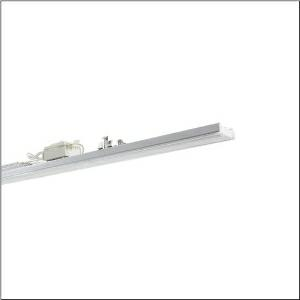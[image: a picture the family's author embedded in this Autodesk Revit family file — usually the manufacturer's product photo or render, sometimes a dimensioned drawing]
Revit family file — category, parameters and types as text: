
# Revit family: licross_r__21_recessed_ho_52te12dn4fxm3s4_e70e
name_source: partatom
category: Lighting Fixtures
units: mm (PartAtom-declared; Revit-internal decimal feet)

## family parameters
Cut with Voids When Loaded = No
Host = Face
Light Source = No
Part Type = Normal
Room Calculation Point = No
Round Connector Dimension = Use Diameter
Shared = No

## types (1)
- --- (1 x LED, 930 lm, 7.5 W, 4000K)
    Apparent Load = 8 VA
    CIE Flux Codes = 69 91 98 100 100
    Color Rendering = 80
    Color Temperature = 4000K
    Default Elevation = 1800 mm
    Description = Licross® 21 Recessed HO, luminaire insert, of sheet steel, galvanised, coil coated, white, length: 1.500mm, width: 66mm, height: 67mm, LED rated luminous flux: 15.000lm, light colour: 840, control gear: DALI 2, with plug, 6-pole, with phase selection, for trunking rail, 9 or 11-core, mains connection: 220..240V, AC, 50/60Hz, rated input power: 88W, internal wiring halogen-free, for emergency light function, for trunking rail, 9-/11-core, converter,control gear: single battery element, battery: LiFePO4, 9Ah, primary optical cover: cover, of PMMA, light emission: direct distribution, primary light characteristic: symmetric, protection rating (complete): IP54, insulation class (complete): insulation class I (protective earthing), certification: CE, UKCA, protection symbol: D if used in an environment with non-conductive dust loads with corresponding accessories, impact resistance: IK06, permissible ambient temperature for indoor applications: +5..+30°C, standard: EN 60598-2-22, LABS conformity tested according to VDMA 24364:2018-05, reducing of maximum allowable ambient temperature of 5°C with ceiling mounting, corresponds to IFS (International Featured Standards) requirements for safety and quality in the food industry, packaging unit: 1 piece
    Height = 58 mm
    Lamp = 1 x LED
    Lamp Light Flux = 930 lm
    Lamp Power = 7.5 W
    Lamp count = 1
    Length = 1500 mm
    Luminous efficacy = 124 lm/W
    Manufacturer = Siteco
    ModVariant = No
    Model = 52TE12DN4FXM3S4
    Mounting Place = Ceiling
    Mounting Type = Pendant
    Number of Poles = 1
    OnlyDefault = Yes
    Power Factor = 1
    Product Name = Licross® 21 Recessed HO
    Product group = luminaire insert | ceiling pendant
    ProductGroupID = 902
    Protection Class = Protection class I
    Protection Degree = IP 54
    RLX_Detail_Level = 1
    RLX_Emergency_Light_Flux = 0 lm
    RLX_Emergency_Type = 0
    RLX_Emergency_Type_DB = No
    RlxData = <blob elided: 25137 chars, md5=6c743dbe>
    Socket = socket
    Standby Power = 0 W
    System Light Flux = 930 lm
    System Power = 8 W
    Type Comments = : emergency light operation: 3 h
    Type Image = l_1296930.jpg
    URL = http://relux.com
    VarID = @adj_130747
    Voltage = 0 V
    Weight = 0.00 kg
    Width = 66 mm

## geometry (parser evidence)
native form markers: Blend x4, Sweep x10
no freeform markers — native parametric forms only
